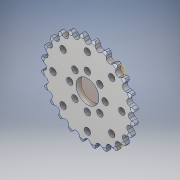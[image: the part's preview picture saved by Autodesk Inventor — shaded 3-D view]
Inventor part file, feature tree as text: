
AUTODESK INVENTOR PART (.ipt)
format: ipt  version: 2017 (Build 210142000, 142)  size: 439,808 bytes
history: native  units: in
note: dims shown in document units (in); Inventor stores cm internally (conversion verified against a paired STEP export)
features: plane x1, pattern_circular x1
ambient origin geometry x8: Origin, YZ Plane, XZ Plane, XY Plane, X Axis, Y Axis, Z Axis, Center Point
bodies: Solid1 (feature_tree)
feature tree (2):
  plane  "Work Plane1"
  pattern_circular  "CirPattern2"
